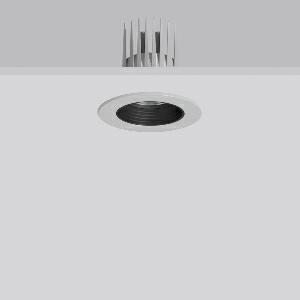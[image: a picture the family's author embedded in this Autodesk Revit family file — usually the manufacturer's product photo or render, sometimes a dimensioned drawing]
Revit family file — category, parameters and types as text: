
# Revit family: heledon_mini_e_901754_004_2_76_c5d6
name_source: partatom
category: Lighting Fixtures
units: mm (PartAtom-declared; Revit-internal decimal feet)

## family parameters
Cut with Voids When Loaded = No
Host = Face
Light Source = No
Part Type = Normal
Room Calculation Point = No
Round Connector Dimension = Use Diameter
Shared = No

## types (1)
- HELEDON mini E (1 x LED Modul 927, 3050 lm, 2700)
    Apparent Load = 29 VA
    Approval mark = CE
    CIE Flux Codes = 80 99 100 100 100
    Color Rendering = 92
    Color Temperature = 2700
    Default Elevation = 1800 mm
    Description = Series: HELEDON mini
Round recessed downlight. Housing: die-cast aluminium, powder-coated. Black plastic ring and recessed LED to prevent glare from the side. Optical assembly with lens made of plastic (polycarbonate) for the best homogeneous light distribution - can be changed without tools. Best colour rendering index Ra>90. Suitable for Recessed ceiling mounting. Installation without tools thanks to spring fastening system. Including separate LED converter with connecting cable 600 mm.High quality converter without flickering and stroboscopic effect. Through-wiring box (5 pole) available as accessory. The following accessories can be mounted without use of tools: interchangeable lenses, decorative glasses, honeycomb louvre, clear and frosted diffusers, white interchangeable plastic ring. 
Colour: silver
Diameter: 124 mm
Height: 3 mm
Cut-out diameter: 114 mm
Recess height: 170 mm
Luminaire: recess height: 120 mm
Lamp: LED
Socket: without socket
Colour temperature: 2700K
Colour rendering index (CRI): 92
System power: 29 W
Rated luminous flux: 3050 lm
Luminous efficiency: 105 lm/W
Control gear: Converter, dimmable, DALI
Protection class: II
Type of protection: IP 20
    Height = 0 mm  [stored 0 ft]
    Lamp = 1 x LED Modul 927
    Lamp Light Flux = 3050 lm
    Lamp count = 1
    Length = 124 mm  [stored 0.406824 ft]
    Lifetime = 50000 h
    Luminous efficacy = 105 lm/W
    Manufacturer = RZB
    ModVariant = No
    Model = 901754.004.2.76
    Mounting Place = Ceiling
    Mounting Type = Recessed
    Number of Poles = 1
    OnlyDefault = Yes
    Power Factor = 1
    Product Name = HELEDON mini E
    Product group = Recessed downlights
    ProductGroupID = 402
    Protection Class = Protection class II
    Protection Degree = IP 20
    RLX_Detail_Level = 1
    RLX_Emergency_Light_Flux = 0 lm
    RLX_Emergency_Type = 0
    RLX_Emergency_Type_DB = No
    RlxData = <blob elided: 124993 chars, md5=64db734e>
    Socket = socket
    Standby Power = 0 W
    System Light Flux = 3050 lm
    System Power = 29 W
    Type Comments = Product without accessories
    Type Image = 901656.004.jpg
    URL = http://relux.com
    VarID = ---
    Voltage = 230 V
    Voltage Range = 220-240 V
    Weight = 0.00 kg
    Width = 0 mm  [stored 0 ft]

note: [stored X ft] marks values corroborated as IEEE doubles in the binary element streams (Revit-internal decimal feet)

## geometry (parser evidence)
native form markers: Blend x4, Sweep x10
no freeform markers — native parametric forms only
